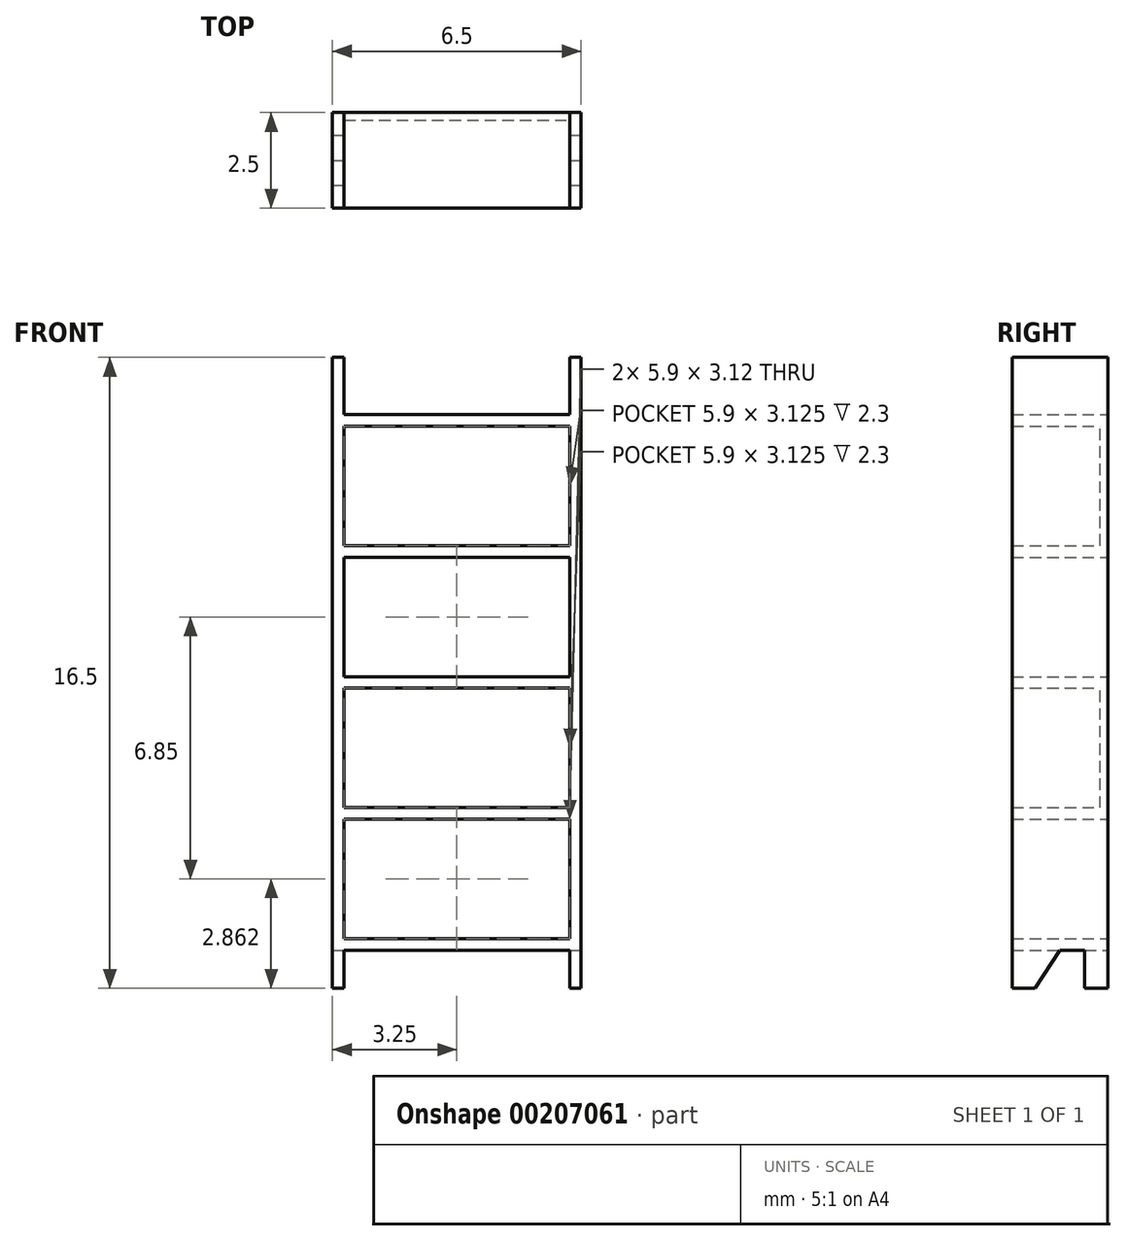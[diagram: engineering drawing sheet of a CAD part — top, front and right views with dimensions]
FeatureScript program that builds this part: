
annotation { "Feature Type Name" : "Feature", "Feature Type Description" : "" }
export const myFeature = defineFeature(function(context is Context, id is Id, definition is map)
    precondition{}
    {
        {
            var Q0;
            Q0=qCreatedBy(makeId("Front.planeOp"),FACE);
            var sketch = newSketch(context, id + "F0", { "sketchPlane" : qUnion([Q0])});
            skLineSegment(sketch, "E0.bottom", {"start": v(-3.25, 0) * mm, "end": v(3.25, 0) * mm});
            skLineSegment(sketch, "E0.top", {"start": v(-3.25, 16.5) * mm, "end": v(3.25, 16.5) * mm});
            skLineSegment(sketch, "E0.left", {"start": v(-3.25, 0) * mm, "end": v(-3.25, 16.5) * mm});
            skLineSegment(sketch, "E0.right", {"start": v(3.25, 0) * mm, "end": v(3.25, 16.5) * mm});
            skLineSegment(sketch, "E1.bottom", {"start": v(-2.95, 0) * mm, "end": v(2.95, 0) * mm});
            skLineSegment(sketch, "E1.top", {"start": v(-2.95, 16.5) * mm, "end": v(2.95, 16.5) * mm});
            skLineSegment(sketch, "E1.left", {"start": v(-2.95, 0) * mm, "end": v(-2.95, 16.5) * mm});
            skLineSegment(sketch, "E1.right", {"start": v(2.95, 0) * mm, "end": v(2.95, 16.5) * mm});
            skLineSegment(sketch, "E2", {"start": v(-2.95, 8.25) * mm, "end": v(-3.25, 8.25) * mm, "construction": true});
            skLineSegment(sketch, "E3", {"start": v(2.95, 8.25) * mm, "end": v(3.25, 8.25) * mm, "construction": true});
            skLineSegment(sketch, "E4.bottom", {"start": v(-2.95, 1) * mm, "end": v(2.95, 1) * mm});
            skLineSegment(sketch, "E4.top", {"start": v(-2.95, 1.3) * mm, "end": v(2.95, 1.3) * mm});
            skLineSegment(sketch, "E4.left", {"start": v(-2.95, 1) * mm, "end": v(-2.95, 1.3) * mm});
            skLineSegment(sketch, "E4.right", {"start": v(2.95, 1) * mm, "end": v(2.95, 1.3) * mm});
            skLineSegment(sketch, "E5.bottom", {"start": v(-2.95, 7.85) * mm, "end": v(2.95, 7.85) * mm});
            skLineSegment(sketch, "E5.top", {"start": v(-2.95, 8.15) * mm, "end": v(2.95, 8.15) * mm});
            skLineSegment(sketch, "E5.left", {"start": v(-2.95, 7.85) * mm, "end": v(-2.95, 8.15) * mm});
            skLineSegment(sketch, "E5.right", {"start": v(2.95, 7.85) * mm, "end": v(2.95, 8.15) * mm});
            skLineSegment(sketch, "E6.bottom", {"start": v(-2.95, 11.28) * mm, "end": v(2.95, 11.28) * mm});
            skLineSegment(sketch, "E6.top", {"start": v(-2.95, 11.58) * mm, "end": v(2.95, 11.58) * mm});
            skLineSegment(sketch, "E6.left", {"start": v(-2.95, 11.28) * mm, "end": v(-2.95, 11.58) * mm});
            skLineSegment(sketch, "E6.right", {"start": v(2.95, 11.27) * mm, "end": v(2.95, 11.57) * mm});
            skLineSegment(sketch, "E7.bottom", {"start": v(-2.95, 14.7) * mm, "end": v(2.95, 14.7) * mm});
            skLineSegment(sketch, "E7.top", {"start": v(-2.95, 15) * mm, "end": v(2.95, 15) * mm});
            skLineSegment(sketch, "E7.left", {"start": v(-2.95, 14.7) * mm, "end": v(-2.95, 15) * mm});
            skLineSegment(sketch, "E7.right", {"start": v(2.95, 14.7) * mm, "end": v(2.95, 15) * mm});
            skLineSegment(sketch, "E8.bottom", {"start": v(-2.95, 4.72) * mm, "end": v(2.95, 4.72) * mm});
            skLineSegment(sketch, "E8.top", {"start": v(-2.95, 4.42) * mm, "end": v(2.95, 4.42) * mm});
            skLineSegment(sketch, "E8.left", {"start": v(-2.95, 4.72) * mm, "end": v(-2.95, 4.42) * mm});
            skLineSegment(sketch, "E8.right", {"start": v(2.95, 4.72) * mm, "end": v(2.95, 4.42) * mm});
            skLineSegment(sketch, "E9", {"start": v(0, 11.58) * mm, "end": v(0, 14.7) * mm, "construction": true});
            skLineSegment(sketch, "E10", {"start": v(0, 11.28) * mm, "end": v(0, 8.15) * mm, "construction": true});
            skLineSegment(sketch, "E11", {"start": v(0, 7.85) * mm, "end": v(0, 4.72) * mm, "construction": true});
            skLineSegment(sketch, "E12", {"start": v(0, 4.42) * mm, "end": v(0, 1.3) * mm, "construction": true});
            skSolve(sketch);
        }
        {
            var Q0;
            {var subQ7=sQuery(id+"F0.wireOp",EDGE,"E0.left");Q0=makeQuery(id+"F0.imprint","IMPRINT",FACE,{"disambiguationData":[TD([[makeQuery(id+"F0.imprint","IMPRINT",EDGE,{"derivedFrom":subQ7}),-1.0]])]});}
            var Q1;
            {var subQ5=sQuery(id+"F0.wireOp",EDGE,"E0.right");Q1=makeQuery(id+"F0.imprint","IMPRINT",FACE,{"disambiguationData":[TD([[makeQuery(id+"F0.imprint","IMPRINT",EDGE,{"derivedFrom":subQ5}),1.0]])]});}
            var Q2;
            Q2=makeQuery(id+"F0.imprint","IMPRINT",FACE,{"disambiguationData":[TD([[makeQuery(id+"F0.imprint","IMPRINT",EDGE,{"derivedFrom":sQuery(id+"F0.wireOp",EDGE,"E7.bottom")}),1.0]])]});
            var Q3;
            Q3=makeQuery(id+"F0.imprint","IMPRINT",FACE,{"disambiguationData":[TD([[makeQuery(id+"F0.imprint","IMPRINT",EDGE,{"derivedFrom":sQuery(id+"F0.wireOp",EDGE,"E6.bottom")}),1.0]])]});
            var Q4;
            Q4=makeQuery(id+"F0.imprint","IMPRINT",FACE,{"disambiguationData":[TD([[makeQuery(id+"F0.imprint","IMPRINT",EDGE,{"derivedFrom":sQuery(id+"F0.wireOp",EDGE,"E5.bottom")}),1.0]])]});
            var Q5;
            Q5=makeQuery(id+"F0.imprint","IMPRINT",FACE,{"disambiguationData":[TD([[makeQuery(id+"F0.imprint","IMPRINT",EDGE,{"derivedFrom":sQuery(id+"F0.wireOp",EDGE,"E8.bottom")}),-1.0]])]});
            var Q6;
            Q6=makeQuery(id+"F0.imprint","IMPRINT",FACE,{"disambiguationData":[TD([[makeQuery(id+"F0.imprint","IMPRINT",EDGE,{"derivedFrom":sQuery(id+"F0.wireOp",EDGE,"E4.bottom")}),1.0]])]});
            extrude(context, id + "F1", {"entities" : qUnion([Q0, Q1, Q2, Q3, Q4, Q5, Q6]), "depth" : 2.5 * mm});
        }
        {
            var Q0;
            {var subQ0=sQuery(id+"F0.wireOp",EDGE,"E6.top");Q0=makeQuery(id+"F0.imprint","IMPRINT",FACE,{"disambiguationData":[TD([[makeQuery(id+"F0.imprint","IMPRINT",EDGE,{"derivedFrom":subQ0}),1.0]])]});}
            var Q1;
            {var subQ0=sQuery(id+"F0.wireOp",EDGE,"E5.bottom");Q1=makeQuery(id+"F0.imprint","IMPRINT",FACE,{"disambiguationData":[TD([[makeQuery(id+"F0.imprint","IMPRINT",EDGE,{"derivedFrom":subQ0}),-1.0]])]});}
            extrude(context, id + "F2", {"entities" : qUnion([Q0, Q1]), "operationType" : NewBodyOperationType.ADD, "depth" : 0.2 * mm});
        }
        {
            var Q0;
            Q0=makeQuery(id+"F1.opExtrude","SWEPT_FACE",FACE,{"disambiguationData":[OSD([sQuery(id+"F0.wireOp",EDGE,"E0.right")])]});
            var sketch = newSketch(context, id + "F3", { "sketchPlane" : qUnion([Q0])});
            skLineSegment(sketch, "E13.bottom", {"start": v(-0.6, 0) * mm, "end": v(-1.9, 0) * mm});
            skLineSegment(sketch, "E13.top", {"start": v(-0.6, 1) * mm, "end": v(-1.9, 1) * mm});
            skLineSegment(sketch, "E13.left", {"start": v(-0.6, 0) * mm, "end": v(-0.6, 1) * mm});
            skLineSegment(sketch, "E13.right", {"start": v(-1.9, 0) * mm, "end": v(-1.9, 1) * mm});
            skLineSegment(sketch, "E14", {"start": v(-1.9, 0.5) * mm, "end": v(-2.5, 0.5) * mm, "construction": true});
            skLineSegment(sketch, "E15", {"start": v(-0.6, 0.5) * mm, "end": v(0, 0.5) * mm, "construction": true});
            skLineSegment(sketch, "E16", {"start": v(-1.9, 0) * mm, "end": v(-1.25, 1) * mm});
            skSolve(sketch);
        }
        {
            var Q0;
            Q0=makeQuery(id+"F3.imprint","IMPRINT",FACE,{"disambiguationData":[TD([[makeQuery(id+"F3.imprint","IMPRINT",EDGE,{"derivedFrom":sQuery(id+"F3.wireOp",EDGE,"E13.bottom")}),1.0]])]});
            extrude(context, id + "F4", {"entities" : qUnion([Q0]), "operationType" : NewBodyOperationType.REMOVE, "endBound" : BoundingType.THROUGH_ALL, "oppositeDirection" : true, "depth" : 25 * mm});
        }
    });
